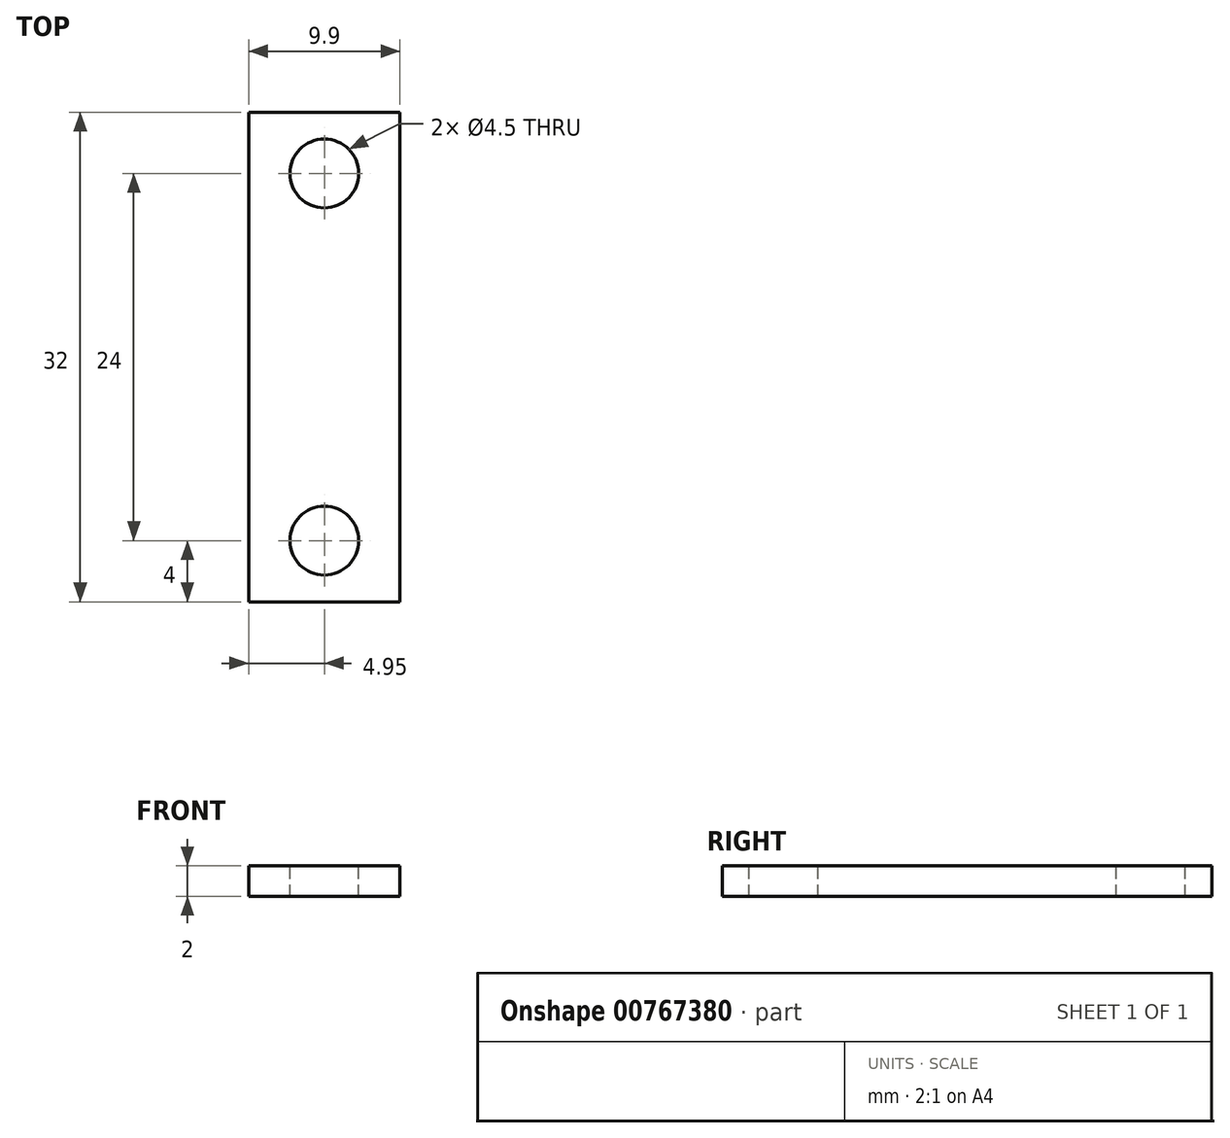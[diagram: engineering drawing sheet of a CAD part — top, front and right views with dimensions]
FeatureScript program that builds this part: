
annotation { "Feature Type Name" : "Feature", "Feature Type Description" : "" }
export const myFeature = defineFeature(function(context is Context, id is Id, definition is map)
    precondition{}
    {
        {
            var Q0;
            Q0=qCreatedBy(makeId("Top.planeOp"),FACE);
            var sketch = newSketch(context, id + "F0", { "sketchPlane" : qUnion([Q0])});
            skLineSegment(sketch, "E0.bottom", {"start": v(4.95, -16) * mm, "end": v(-4.95, -16) * mm});
            skLineSegment(sketch, "E0.top", {"start": v(4.95, 16) * mm, "end": v(-4.95, 16) * mm});
            skLineSegment(sketch, "E0.left", {"start": v(4.95, -16) * mm, "end": v(4.95, 16) * mm});
            skLineSegment(sketch, "E0.right", {"start": v(-4.95, -16) * mm, "end": v(-4.95, 16) * mm});
            skPoint(sketch, "E0.middle", {"position": v(0, 0) * mm});
            skSolve(sketch);
        }
        {
            var Q0;
            Q0=makeQuery(id+"F0.imprint","IMPRINT",FACE,{"disambiguationData":[TD([[makeQuery(id+"F0.imprint","IMPRINT",EDGE,{"derivedFrom":sQuery(id+"F0.wireOp",EDGE,"E0.bottom")}),-1.0]])]});
            extrude(context, id + "F1", {"entities" : qUnion([Q0]), "depth" : 2 * mm, "offsetDistance" : 25 * mm});
        }
        {
            var Q0;
            Q0=makeQuery(id+"F1.opExtrude","CAP_FACE",FACE,{"disambiguationData":[OSD([sQuery(id+"F0.wireOp",EDGE,"E0.bottom"),sQuery(id+"F0.wireOp",EDGE,"E0.top"),sQuery(id+"F0.wireOp",EDGE,"E0.left"),sQuery(id+"F0.wireOp",EDGE,"E0.right")])],"isStart":false});
            var sketch = newSketch(context, id + "F2", { "sketchPlane" : qUnion([Q0])});
            skCircle(sketch, "E1", {"center": v(0, 12) * mm, "radius": 2.25 * mm});
            skPoint(sketch, "E1.centerSnap0", {"position": v(0, 16) * mm});
            skCircle(sketch, "E2", {"center": v(0, -12) * mm, "radius": 2.25 * mm});
            skSolve(sketch);
        }
        {
            var Q0;
            Q0=makeQuery(id+"F2.imprint","IMPRINT",FACE,{"disambiguationData":[TD([[makeQuery(id+"F2.imprint","IMPRINT",EDGE,{"derivedFrom":sQuery(id+"F2.wireOp",EDGE,"E1")}),1.0]])]});
            var Q1;
            Q1=makeQuery(id+"F2.imprint","IMPRINT",FACE,{"disambiguationData":[TD([[makeQuery(id+"F2.imprint","IMPRINT",EDGE,{"derivedFrom":sQuery(id+"F2.wireOp",EDGE,"E2")}),1.0]])]});
            extrude(context, id + "F3", {"entities" : qUnion([Q0, Q1]), "operationType" : NewBodyOperationType.REMOVE, "oppositeDirection" : true, "depth" : 25 * mm, "offsetDistance" : 25 * mm});
        }
    });
